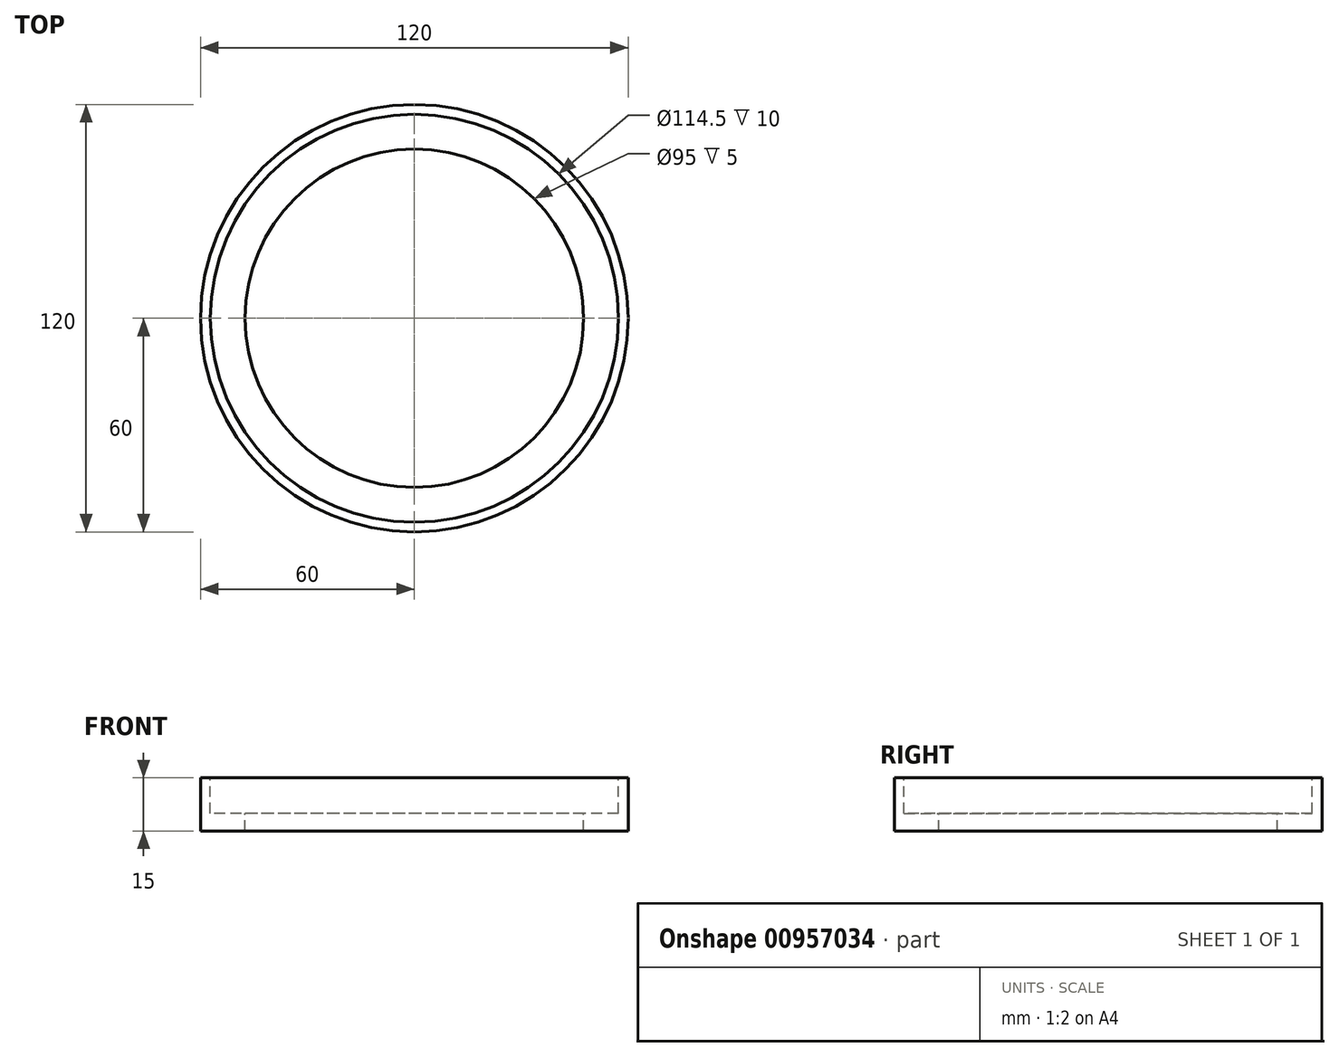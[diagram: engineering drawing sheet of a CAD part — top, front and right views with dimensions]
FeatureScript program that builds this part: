
annotation { "Feature Type Name" : "Feature", "Feature Type Description" : "" }
export const myFeature = defineFeature(function(context is Context, id is Id, definition is map)
    precondition{}
    {
        {
            var Q0;
            Q0=qCreatedBy(makeId("Front.planeOp"),FACE);
            var sketch = newSketch(context, id + "F0", { "sketchPlane" : qUnion([Q0])});
            skLineSegment(sketch, "E0", {"start": v(60, 15) * mm, "end": v(60, 0) * mm});
            skLineSegment(sketch, "E1", {"start": v(60, 15) * mm, "end": v(57.25, 15) * mm});
            skLineSegment(sketch, "E2", {"start": v(57.25, 15) * mm, "end": v(57.25, 5) * mm});
            skLineSegment(sketch, "E3", {"start": v(57.25, 5) * mm, "end": v(47.5, 5) * mm});
            skLineSegment(sketch, "E4", {"start": v(47.5, 5) * mm, "end": v(47.5, 0) * mm});
            skLineSegment(sketch, "E5", {"start": v(47.5, 0) * mm, "end": v(60, 0) * mm});
            skLineSegment(sketch, "E6", {"start": v(0, 66.4) * mm, "end": v(0, -67.67) * mm, "construction": true});
            skSolve(sketch);
        }
        {
            var Q0;
            Q0 = qSketchRegion(id + "F0", true);
            var Q1;
            Q1=sQuery(id+"F0.wireOp",EDGE,"E6");
            revolve(context, id + "F1", {"surfaceOperationType" : NewSurfaceOperationType.NEW, "entities" : qUnion([Q0]), "axis" : qUnion([Q1]), "revolveType" : RevolveType.FULL});
        }
    });
